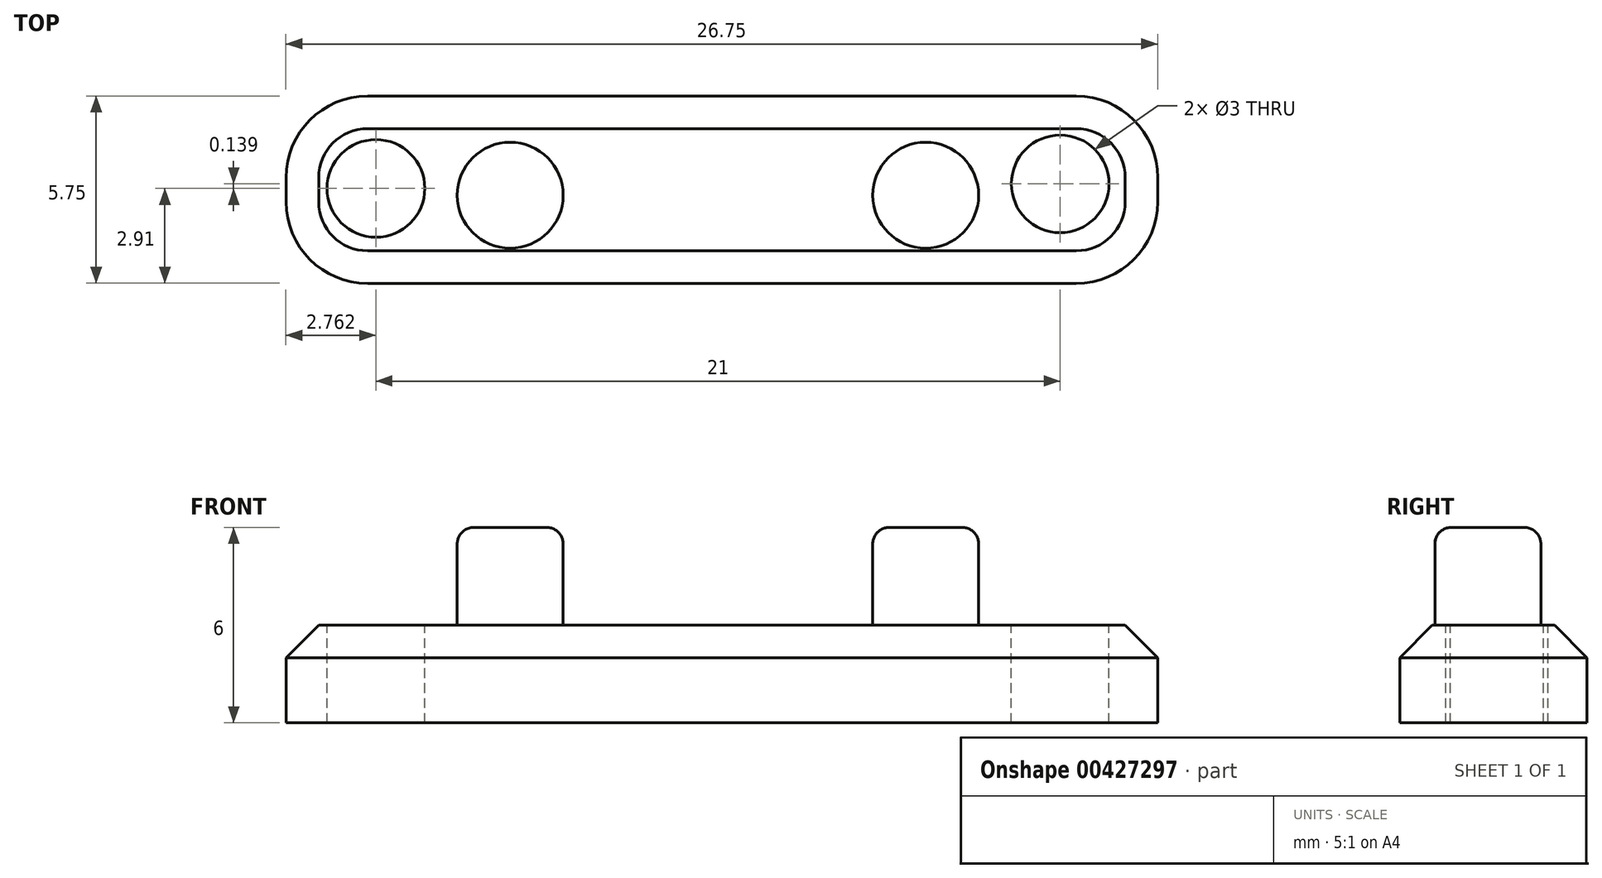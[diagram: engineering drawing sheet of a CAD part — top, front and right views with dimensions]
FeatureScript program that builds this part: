
annotation { "Feature Type Name" : "Feature", "Feature Type Description" : "" }
export const myFeature = defineFeature(function(context is Context, id is Id, definition is map)
    precondition{}
    {
        {
            var Q0;
            Q0=qCreatedBy(makeId("Top.planeOp"),FACE);
            var sketch = newSketch(context, id + "F0", { "sketchPlane" : qUnion([Q0])});
            skLineSegment(sketch, "E0.bottom", {"start": v(-13.87, 11.47) * mm, "end": v(7.88, 11.47) * mm});
            skLineSegment(sketch, "E0.top", {"start": v(-13.87, 5.72) * mm, "end": v(7.88, 5.72) * mm});
            skLineSegment(sketch, "E0.left", {"start": v(-16.37, 8.97) * mm, "end": v(-16.37, 8.22) * mm});
            skLineSegment(sketch, "E0.right", {"start": v(10.38, 8.97) * mm, "end": v(10.38, 8.22) * mm});
            skPoint(sketch, "E1.visualSharp", {"position": v(-16.37, 11.47) * mm});
            skArc(sketch, "E1.filletArc", {"start": v(-13.87, 11.47) * mm, "mid": v(-15.63, 10.73) * mm, "end": v(-16.37, 8.97) * mm});
            skPoint(sketch, "E2.visualSharp", {"position": v(-16.37, 5.72) * mm});
            skArc(sketch, "E2.filletArc", {"start": v(-16.37, 8.22) * mm, "mid": v(-15.63, 6.45) * mm, "end": v(-13.87, 5.72) * mm});
            skPoint(sketch, "E3.visualSharp", {"position": v(10.38, 5.72) * mm});
            skArc(sketch, "E3.filletArc", {"start": v(7.88, 5.72) * mm, "mid": v(9.65, 6.45) * mm, "end": v(10.38, 8.22) * mm});
            skPoint(sketch, "E4.visualSharp", {"position": v(10.38, 11.47) * mm});
            skArc(sketch, "E4.filletArc", {"start": v(10.38, 8.97) * mm, "mid": v(9.65, 10.73) * mm, "end": v(7.88, 11.47) * mm});
            skSolve(sketch);
        }
        {
            var Q0;
            Q0=makeQuery(id+"F0.imprint","IMPRINT",FACE,{"disambiguationData":[TD([[makeQuery(id+"F0.imprint","IMPRINT",EDGE,{"derivedFrom":sQuery(id+"F0.wireOp",EDGE,"E0.bottom")}),-1.0]])]});
            extrude(context, id + "F1", {"entities" : qUnion([Q0]), "depth" : 3 * mm});
        }
        {
            var Q0;
            Q0=makeQuery(id+"F1.opExtrude","CAP_FACE",FACE,{"disambiguationData":[OSD([sQuery(id+"F0.wireOp",EDGE,"E0.bottom"),sQuery(id+"F0.wireOp",EDGE,"E0.top"),sQuery(id+"F0.wireOp",EDGE,"E0.left"),sQuery(id+"F0.wireOp",EDGE,"E0.right"),sQuery(id+"F0.wireOp",EDGE,"E1.filletArc"),sQuery(id+"F0.wireOp",EDGE,"E2.filletArc"),sQuery(id+"F0.wireOp",EDGE,"E3.filletArc"),sQuery(id+"F0.wireOp",EDGE,"E4.filletArc")])],"isStart":false});
            var sketch = newSketch(context, id + "F2", { "sketchPlane" : qUnion([Q0])});
            skCircle(sketch, "E5", {"center": v(-9.49, 8.42) * mm, "radius": 1.63 * mm});
            skCircle(sketch, "E6", {"center": v(3.26, 8.42) * mm, "radius": 1.63 * mm});
            skCircle(sketch, "E7", {"center": v(7.4, 8.77) * mm, "radius": 1.5 * mm});
            skCircle(sketch, "E8", {"center": v(-13.6, 8.63) * mm, "radius": 1.5 * mm});
            skSolve(sketch);
        }
        {
            var Q0;
            Q0=makeQuery(id+"F2.imprint","IMPRINT",FACE,{"disambiguationData":[TD([[makeQuery(id+"F2.imprint","IMPRINT",EDGE,{"derivedFrom":sQuery(id+"F2.wireOp",EDGE,"E5")}),1.0]])]});
            var Q1;
            Q1=makeQuery(id+"F2.imprint","IMPRINT",FACE,{"disambiguationData":[TD([[makeQuery(id+"F2.imprint","IMPRINT",EDGE,{"derivedFrom":sQuery(id+"F2.wireOp",EDGE,"E6")}),1.0]])]});
            extrude(context, id + "F3", {"entities" : qUnion([Q0, Q1]), "operationType" : NewBodyOperationType.ADD, "depth" : 3 * mm});
        }
        {
            var Q0;
            Q0=makeQuery(id+"F2.imprint","IMPRINT",FACE,{"disambiguationData":[TD([[makeQuery(id+"F2.imprint","IMPRINT",EDGE,{"derivedFrom":sQuery(id+"F2.wireOp",EDGE,"E8")}),1.0]])]});
            var Q1;
            Q1=makeQuery(id+"F2.imprint","IMPRINT",FACE,{"disambiguationData":[TD([[makeQuery(id+"F2.imprint","IMPRINT",EDGE,{"derivedFrom":sQuery(id+"F2.wireOp",EDGE,"E7")}),1.0]])]});
            extrude(context, id + "F4", {"entities" : qUnion([Q0, Q1]), "operationType" : NewBodyOperationType.REMOVE, "endBound" : BoundingType.SYMMETRIC, "oppositeDirection" : true, "depth" : 25 * mm});
        }
        {
            var Q0;
            Q0=makeQuery(id+"F3.opExtrude","CAP_FACE",FACE,{"disambiguationData":[OSD([sQuery(id+"F2.wireOp",EDGE,"E6")])],"isStart":false});
            var Q1;
            Q1=makeQuery(id+"F3.opExtrude","CAP_FACE",FACE,{"disambiguationData":[OSD([sQuery(id+"F2.wireOp",EDGE,"E5")])],"isStart":false});
            fillet(context, id + "F5", {"entities" : qUnion([Q0, Q1]), "radius" : 0.5 * mm, "tangentPropagation" : true, "allowEdgeOverflow" : false});
        }
        {
            var Q0;
            Q0=makeQuery(id+"F1.opExtrude","CAP_EDGE",EDGE,{"disambiguationData":[OSD([sQuery(id+"F0.wireOp",EDGE,"E0.bottom")])],"isStart":false});
            var Q1;
            Q1=makeQuery(id+"F1.opExtrude","CAP_EDGE",EDGE,{"disambiguationData":[OSD([sQuery(id+"F0.wireOp",EDGE,"E4.filletArc")])],"isStart":false});
            var Q2;
            Q2=makeQuery(id+"F1.opExtrude","CAP_EDGE",EDGE,{"disambiguationData":[OSD([sQuery(id+"F0.wireOp",EDGE,"E1.filletArc")])],"isStart":false});
            var Q3;
            Q3=makeQuery(id+"F1.opExtrude","CAP_EDGE",EDGE,{"disambiguationData":[OSD([sQuery(id+"F0.wireOp",EDGE,"E0.right")])],"isStart":false});
            var Q4;
            Q4=makeQuery(id+"F1.opExtrude","CAP_EDGE",EDGE,{"disambiguationData":[OSD([sQuery(id+"F0.wireOp",EDGE,"E3.filletArc")])],"isStart":false});
            var Q5;
            Q5=makeQuery(id+"F1.opExtrude","CAP_EDGE",EDGE,{"disambiguationData":[OSD([sQuery(id+"F0.wireOp",EDGE,"E0.top")])],"isStart":false});
            var Q6;
            Q6=makeQuery(id+"F1.opExtrude","CAP_EDGE",EDGE,{"disambiguationData":[OSD([sQuery(id+"F0.wireOp",EDGE,"E0.left")])],"isStart":false});
            var Q7;
            Q7=makeQuery(id+"F1.opExtrude","CAP_EDGE",EDGE,{"disambiguationData":[OSD([sQuery(id+"F0.wireOp",EDGE,"E2.filletArc")])],"isStart":false});
            chamfer(context, id + "F6", {"entities" : qUnion([Q0, Q1, Q2, Q3, Q4, Q5, Q6, Q7]), "width" : 1 * mm, "tangentPropagation" : true});
        }
    });
